# Revit family: Zumtobel CROSSIGN - AB
name_source: partatom
category: Lighting Fixtures
revit_build: Autodesk Revit 2014 (Build: 20140709_2115(x64)
units: mm (PartAtom-declared; Revit-internal decimal feet)

## types (10) — shared parameters
Assembly Code = D5020200
Body = Zumtobel_Metal_White
Color Filter = 16777215
Description = Escape sign + ERI LED luminaire
Dimming Lamp Color Temperature Shift = <None>
Lamp = LED
Manufacturer = Zumtobel Lighting
Tilt Angle = 180.00°
URL = http://www.zumtobel.com
Voltage = 230 V
zero-valued in all types: Default Elevation

## per-type parameters (varying)
| type | Apparent Load | Crosign 110 | Crossign 160 | Depth | Escape Bottom | Escape Bottom Left & Right | Escape Left & Right | Escape Top | Escape Top Left & Right | Height | Model | Photometric Web File | Width |
| CROSSIGN 160 AB + RZ-U | 6 VA | No | Yes | 44 mm  [stored 0.144357 ft] | Yes | No | No | No | No | 210 mm | 42180793 + 22168597 | 42180768+22168595_(STD-LEO).IES | 332 mm  [stored 1.08924 ft] |
| CROSSIGN 160 AB + RZ-LRU | 4 VA | No | Yes | 44 mm  [stored 0.144357 ft] | No | Yes | No | No | No | 210 mm | 42180793 + 22900370 | 42180793+22168595_(STD).IES | 332 mm  [stored 1.08924 ft] |
| CROSSIGN 160 AB + RZ-LRO | 4 VA | No | Yes | 44 mm  [stored 0.144357 ft] | No | No | No | No | Yes | 210 mm | 42180793 + 22900369 | 42180793+22168595_(STD).IES | 332 mm  [stored 1.08924 ft] |
| CROSSIGN 110 AB + RZ-LRU | 5 VA | Yes | No | 46 mm  [stored 0.150919 ft] | No | Yes | No | No | No | 176 mm | 42180803 + 22900360 | 42180803+22168605_(STD).IES | 232 mm  [stored 0.761155 ft] |
| CROSSIGN 110 AB + RZ-LRO | 5 VA | Yes | No | 46 mm  [stored 0.150919 ft] | No | No | No | No | Yes | 176 mm | 42180803 + 22900359 | 42180803+22168605_(STD).IES | 232 mm  [stored 0.761155 ft] |
| CROSSIGN 110 AB + RZ-U | 5 VA | Yes | No | 46 mm  [stored 0.150919 ft] | Yes | No | No | No | No | 176 mm | 42180803 + 22168607 | 42180803+22168605_(STD).IES | 232 mm  [stored 0.761155 ft] |
| CROSSIGN 110 AB + RZ-LR | 5 VA | Yes | No | 46 mm  [stored 0.150919 ft] | No | No | Yes | No | No | 176 mm | 42180803 + 22168608 | 42180803+22168605_(STD).IES | 232 mm  [stored 0.761155 ft] |
| CROSSIGN 110 AB + RZ-O | 5 VA | Yes | No | 46 mm  [stored 0.150919 ft] | No | No | No | Yes | No | 176 mm | 42180803 + 22900361 | 42180803+22168605_(STD).IES | 232 mm  [stored 0.761155 ft] |
| CROSSIGN 160 AB + RZ-LR | 4 VA | No | Yes | 44 mm  [stored 0.144357 ft] | No | No | Yes | No | No | 210 mm | 42180793 + 22168598 | 42180793+22168595_(STD).IES | 332 mm  [stored 1.08924 ft] |
| CROSSIGN 160 AB + RZ-O | 6 VA | No | Yes | 44 mm  [stored 0.144357 ft] | No | No | No | Yes | No | 210 mm | 42180793 + 22900364 | 42180768+22168595_(STD-LEO).IES | 332 mm  [stored 1.08924 ft] |

note: [stored X ft] marks values corroborated as IEEE doubles in the binary element streams (Revit-internal decimal feet)

## geometry (parser evidence)
native form markers: Sweep x9
no freeform markers — native parametric forms only
